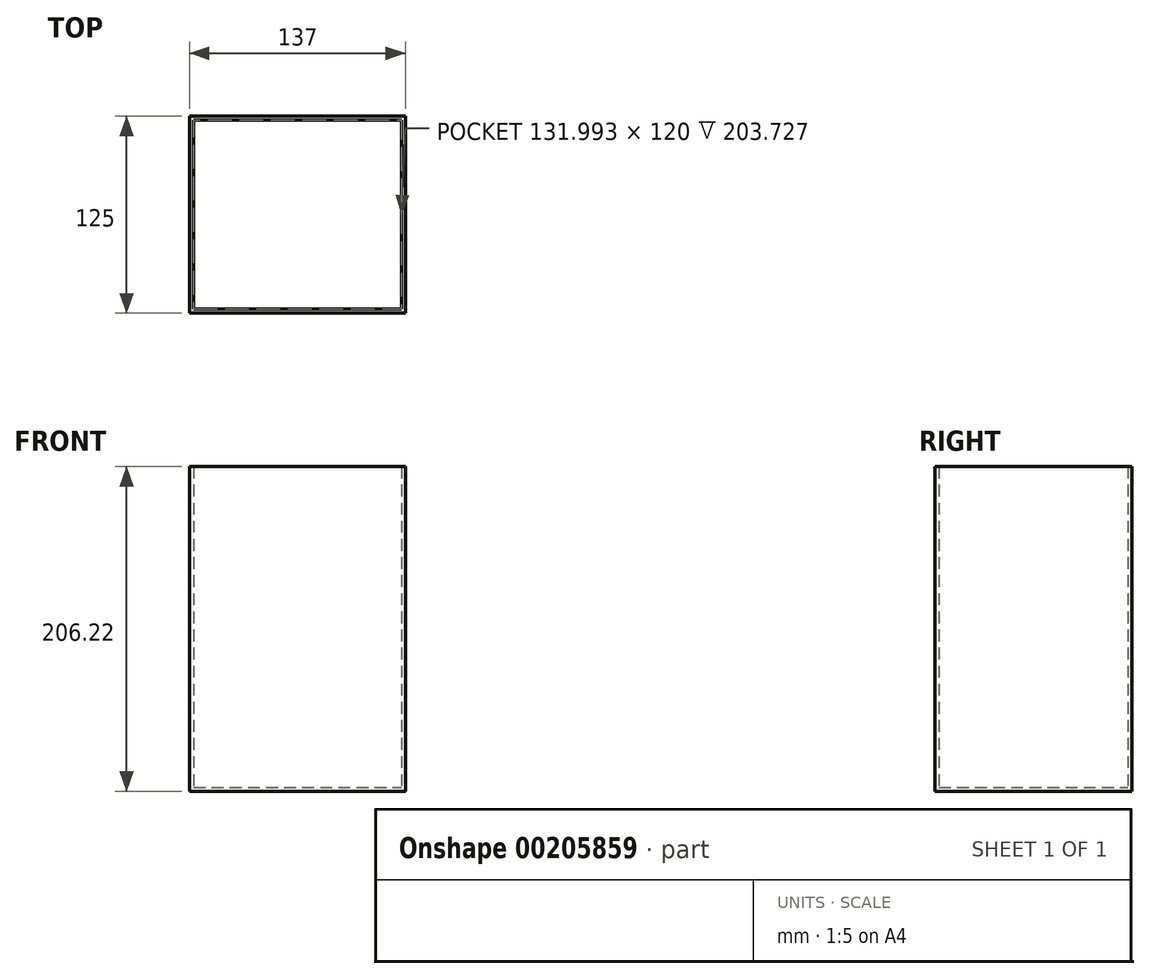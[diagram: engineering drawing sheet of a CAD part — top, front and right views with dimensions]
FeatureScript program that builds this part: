
annotation { "Feature Type Name" : "Feature", "Feature Type Description" : "" }
export const myFeature = defineFeature(function(context is Context, id is Id, definition is map)
    precondition{}
    {
        {
            var Q0;
            Q0=qCreatedBy(makeId("Front.planeOp"),FACE);
            var sketch = newSketch(context, id + "F0", { "sketchPlane" : qUnion([Q0])});
            skLineSegment(sketch, "E0.bottom", {"start": v(-68.5, 49.11) * mm, "end": v(68.5, 49.11) * mm});
            skLineSegment(sketch, "E0.top", {"start": v(-68.5, -49.11) * mm, "end": v(68.5, -49.11) * mm});
            skLineSegment(sketch, "E0.left", {"start": v(-68.5, 49.11) * mm, "end": v(-68.5, -49.11) * mm});
            skLineSegment(sketch, "E0.right", {"start": v(68.5, 49.11) * mm, "end": v(68.5, -49.11) * mm});
            skPoint(sketch, "E0.middle", {"position": v(0, 0) * mm});
            skSolve(sketch);
        }
        {
            var Q0;
            Q0=makeQuery(id+"F0.imprint","IMPRINT",FACE,{"disambiguationData":[TD([[makeQuery(id+"F0.imprint","IMPRINT",EDGE,{"derivedFrom":sQuery(id+"F0.wireOp",EDGE,"E0.bottom")}),-1.0]])]});
            extrude(context, id + "F1", {"entities" : qUnion([Q0]), "depth" : 125 * mm});
        }
        {
            var Q0;
            Q0=makeQuery(id+"F1.opExtrude","SWEPT_FACE",FACE,{"disambiguationData":[OSD([sQuery(id+"F0.wireOp",EDGE,"E0.bottom")])]});
            extrude(context, id + "F2", {"entities" : qUnion([Q0]), "operationType" : NewBodyOperationType.ADD, "depth" : 108 * mm});
        }
        {
            var Q0;
            Q0=makeQuery(id+"F2.opExtrude","CAP_FACE",FACE,{"disambiguationData":[OSD([sQuery(id+"F0.wireOp",EDGE,"E0.bottom")])],"isStart":false});
            shell(context, id + "F3", {"entities" : qUnion([Q0]), "thickness" : 2.5 * mm});
        }
    });
